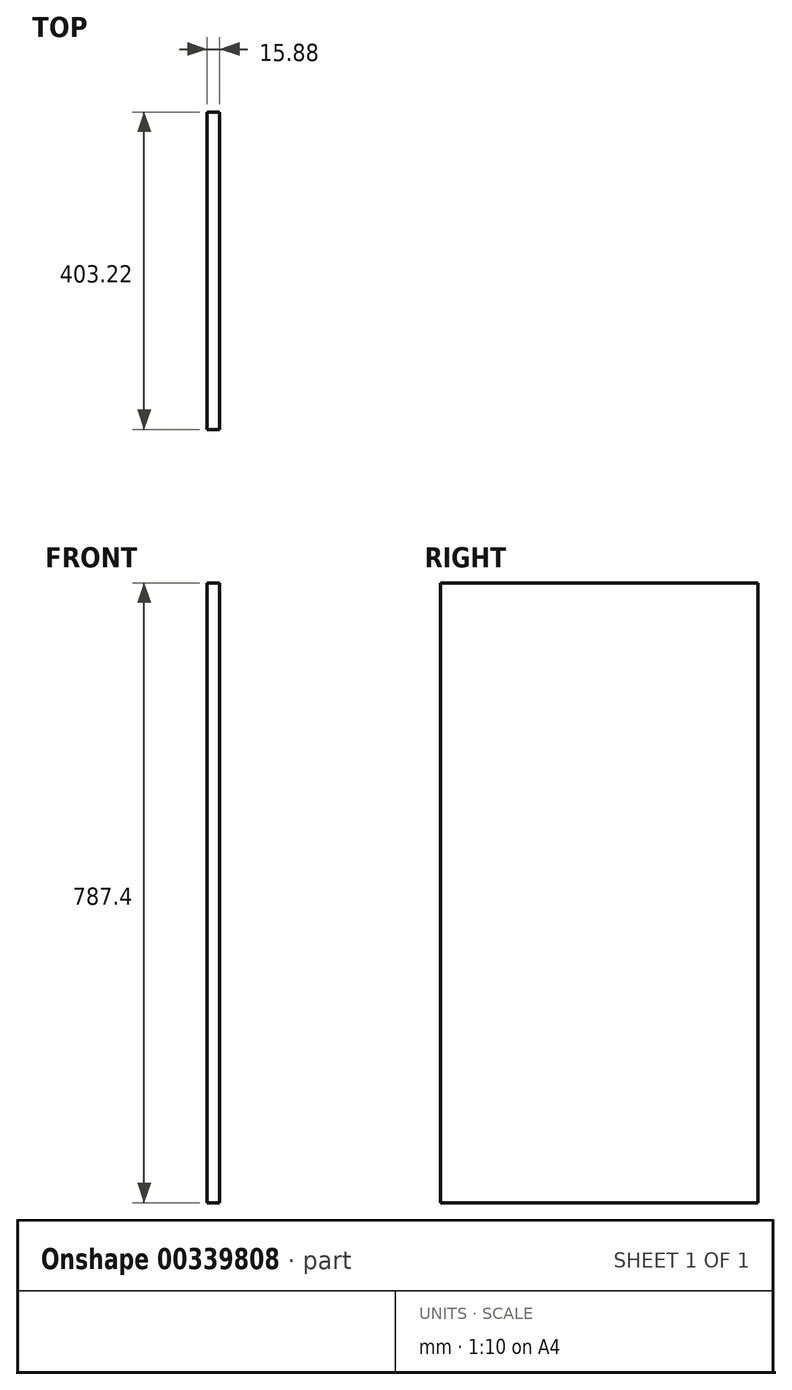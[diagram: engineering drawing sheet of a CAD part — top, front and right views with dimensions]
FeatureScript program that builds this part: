
annotation { "Feature Type Name" : "Feature", "Feature Type Description" : "" }
export const myFeature = defineFeature(function(context is Context, id is Id, definition is map)
    precondition{}
    {
        {
            var Q0;
            Q0=qCreatedBy(makeId("Right.planeOp"),FACE);
            var sketch = newSketch(context, id + "F0", { "sketchPlane" : qUnion([Q0])});
            skLineSegment(sketch, "E0.bottom", {"start": v(-83.81, 694.37) * mm, "end": v(319.41, 694.37) * mm});
            skLineSegment(sketch, "E0.top", {"start": v(-83.81, -93.03) * mm, "end": v(319.41, -93.03) * mm});
            skLineSegment(sketch, "E0.left", {"start": v(-83.81, 694.37) * mm, "end": v(-83.81, -93.03) * mm});
            skLineSegment(sketch, "E0.right", {"start": v(319.41, 694.37) * mm, "end": v(319.41, -93.03) * mm});
            skSolve(sketch);
        }
        {
            var Q0;
            Q0 = qSketchRegion(id + "F0", true);
            extrude(context, id + "F1", {"entities" : qUnion([Q0]), "depth" : 15.88 * mm});
        }
    });
